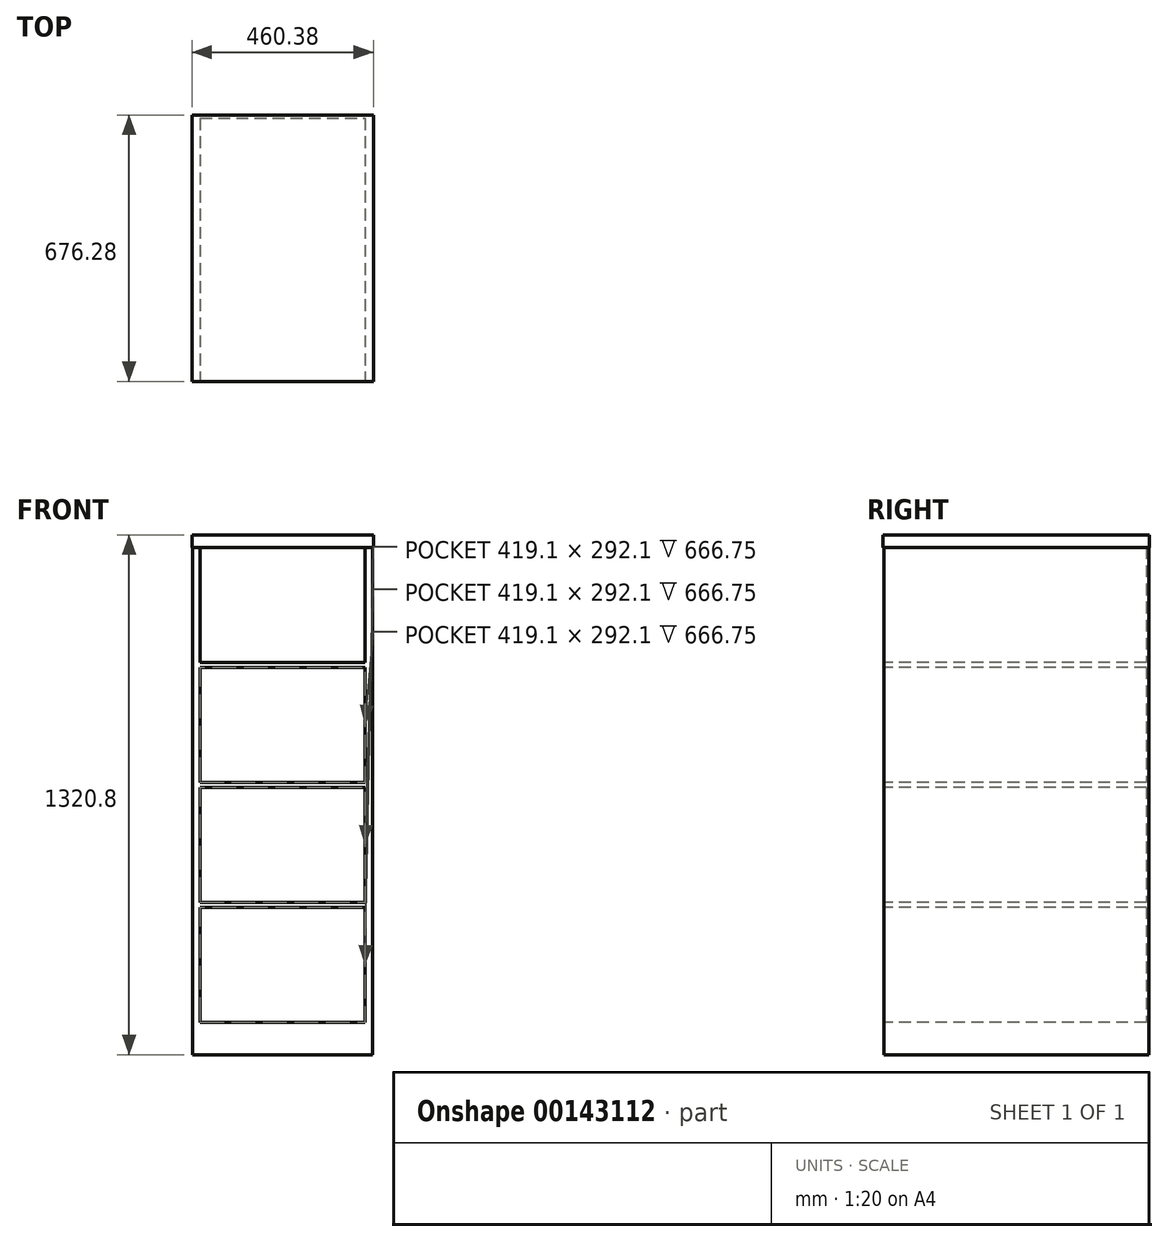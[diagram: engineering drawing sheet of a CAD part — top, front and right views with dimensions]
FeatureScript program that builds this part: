
annotation { "Feature Type Name" : "Feature", "Feature Type Description" : "" }
export const myFeature = defineFeature(function(context is Context, id is Id, definition is map)
    precondition{}
    {
        {
            var Q0;
            Q0=qCreatedBy(makeId("Top.planeOp"),FACE);
            var sketch = newSketch(context, id + "F0", { "sketchPlane" : qUnion([Q0])});
            skLineSegment(sketch, "E0.bottom", {"start": v(0, 0) * mm, "end": v(457.2, 0) * mm});
            skLineSegment(sketch, "E0.top", {"start": v(0, -673.1) * mm, "end": v(457.2, -673.1) * mm});
            skLineSegment(sketch, "E0.left", {"start": v(0, 0) * mm, "end": v(0, -673.1) * mm});
            skLineSegment(sketch, "E0.right", {"start": v(457.2, 0) * mm, "end": v(457.2, -673.1) * mm});
            skSolve(sketch);
        }
        {
            var Q0;
            Q0=makeQuery(id+"F0.imprint","IMPRINT",FACE,{"disambiguationData":[TD([[makeQuery(id+"F0.imprint","IMPRINT",EDGE,{"derivedFrom":sQuery(id+"F0.wireOp",EDGE,"E0.bottom")}),-1.0]])]});
            extrude(context, id + "F1", {"entities" : qUnion([Q0]), "depth" : 1289.05 * mm});
        }
        {
            var Q0;
            Q0=makeQuery(id+"F1.opExtrude","CAP_FACE",FACE,{"disambiguationData":[OSD([sQuery(id+"F0.wireOp",EDGE,"E0.bottom"),sQuery(id+"F0.wireOp",EDGE,"E0.top"),sQuery(id+"F0.wireOp",EDGE,"E0.left"),sQuery(id+"F0.wireOp",EDGE,"E0.right")])],"isStart":false});
            var sketch = newSketch(context, id + "F2", { "sketchPlane" : qUnion([Q0])});
            skLineSegment(sketch, "E1.0", {"start": v(0, -673.1) * mm, "end": v(457.2, -673.1) * mm});
            skLineSegment(sketch, "E2.0", {"start": v(0, 0) * mm, "end": v(0, -673.1) * mm});
            skLineSegment(sketch, "E3.bottom", {"start": v(-1.59, 1.59) * mm, "end": v(458.79, 1.59) * mm});
            skLineSegment(sketch, "E3.top", {"start": v(-1.59, -674.69) * mm, "end": v(458.79, -674.69) * mm});
            skLineSegment(sketch, "E3.left", {"start": v(-1.59, 1.59) * mm, "end": v(-1.59, -674.69) * mm});
            skLineSegment(sketch, "E3.right", {"start": v(458.79, 1.59) * mm, "end": v(458.79, -674.69) * mm});
            skSolve(sketch);
        }
        {
            var Q0;
            Q0=makeQuery(id+"F2.imprint","IMPRINT",FACE,{"disambiguationData":[TD([[makeQuery(id+"F2.imprint","IMPRINT",EDGE,{"derivedFrom":sQuery(id+"F2.wireOp",EDGE,"E1.0")}),-1.0]])]});
            var Q1;
            Q1=makeQuery(id+"F2.imprint","IMPRINT",FACE,{"disambiguationData":[TD([[makeQuery(id+"F2.imprint","IMPRINT",EDGE,{"derivedFrom":sQuery(id+"F2.wireOp",EDGE,"E1.0")}),1.0]])]});
            extrude(context, id + "F3", {"entities" : qUnion([Q0, Q1]), "operationType" : NewBodyOperationType.ADD, "depth" : 31.75 * mm});
        }
        {
            var Q0;
            Q0=makeQuery(id+"F1.opExtrude","SWEPT_FACE",FACE,{"disambiguationData":[OSD([sQuery(id+"F0.wireOp",EDGE,"E0.top")])]});
            var sketch = newSketch(context, id + "F4", { "sketchPlane" : qUnion([Q0])});
            skLineSegment(sketch, "E4.bottom", {"start": v(19.05, 1289.05) * mm, "end": v(438.15, 1289.05) * mm});
            skLineSegment(sketch, "E4.top", {"start": v(19.05, 996.95) * mm, "end": v(438.15, 996.95) * mm});
            skLineSegment(sketch, "E4.left", {"start": v(19.05, 1289.05) * mm, "end": v(19.05, 996.95) * mm});
            skLineSegment(sketch, "E4.right", {"start": v(438.15, 1289.05) * mm, "end": v(438.15, 996.95) * mm});
            skLineSegment(sketch, "E5.bottom", {"start": v(19.05, 984.25) * mm, "end": v(438.15, 984.25) * mm});
            skLineSegment(sketch, "E5.top", {"start": v(19.05, 692.15) * mm, "end": v(438.15, 692.15) * mm});
            skLineSegment(sketch, "E5.left", {"start": v(19.05, 984.25) * mm, "end": v(19.05, 692.15) * mm});
            skLineSegment(sketch, "E5.right", {"start": v(438.15, 984.25) * mm, "end": v(438.15, 692.15) * mm});
            skLineSegment(sketch, "E6.bottom", {"start": v(19.05, 679.45) * mm, "end": v(438.15, 679.45) * mm});
            skLineSegment(sketch, "E6.top", {"start": v(19.05, 387.35) * mm, "end": v(438.15, 387.35) * mm});
            skLineSegment(sketch, "E6.left", {"start": v(19.05, 679.45) * mm, "end": v(19.05, 387.35) * mm});
            skLineSegment(sketch, "E6.right", {"start": v(438.15, 679.45) * mm, "end": v(438.15, 387.35) * mm});
            skLineSegment(sketch, "E7.bottom", {"start": v(19.05, 374.65) * mm, "end": v(438.15, 374.65) * mm});
            skLineSegment(sketch, "E7.top", {"start": v(19.05, 82.55) * mm, "end": v(438.15, 82.55) * mm});
            skLineSegment(sketch, "E7.left", {"start": v(19.05, 374.65) * mm, "end": v(19.05, 82.55) * mm});
            skLineSegment(sketch, "E7.right", {"start": v(438.15, 374.65) * mm, "end": v(438.15, 82.55) * mm});
            skLineSegment(sketch, "E8.0", {"start": v(457.2, 1289.05) * mm, "end": v(457.2, 0) * mm});
            skSolve(sketch);
        }
        {
            var Q0;
            Q0=makeQuery(id+"F4.imprint","IMPRINT",FACE,{"disambiguationData":[TD([[makeQuery(id+"F4.imprint","IMPRINT",EDGE,{"derivedFrom":sQuery(id+"F4.wireOp",EDGE,"E4.bottom")}),-1.0]])]});
            var Q1;
            Q1=makeQuery(id+"F4.imprint","IMPRINT",FACE,{"disambiguationData":[TD([[makeQuery(id+"F4.imprint","IMPRINT",EDGE,{"derivedFrom":sQuery(id+"F4.wireOp",EDGE,"E5.bottom")}),-1.0]])]});
            var Q2;
            Q2=makeQuery(id+"F4.imprint","IMPRINT",FACE,{"disambiguationData":[TD([[makeQuery(id+"F4.imprint","IMPRINT",EDGE,{"derivedFrom":sQuery(id+"F4.wireOp",EDGE,"E6.bottom")}),-1.0]])]});
            var Q3;
            Q3=makeQuery(id+"F4.imprint","IMPRINT",FACE,{"disambiguationData":[TD([[makeQuery(id+"F4.imprint","IMPRINT",EDGE,{"derivedFrom":sQuery(id+"F4.wireOp",EDGE,"E7.bottom")}),-1.0]])]});
            extrude(context, id + "F5", {"entities" : qUnion([Q0, Q1, Q2, Q3]), "operationType" : NewBodyOperationType.REMOVE, "oppositeDirection" : true, "depth" : 666.75 * mm});
        }
    });
